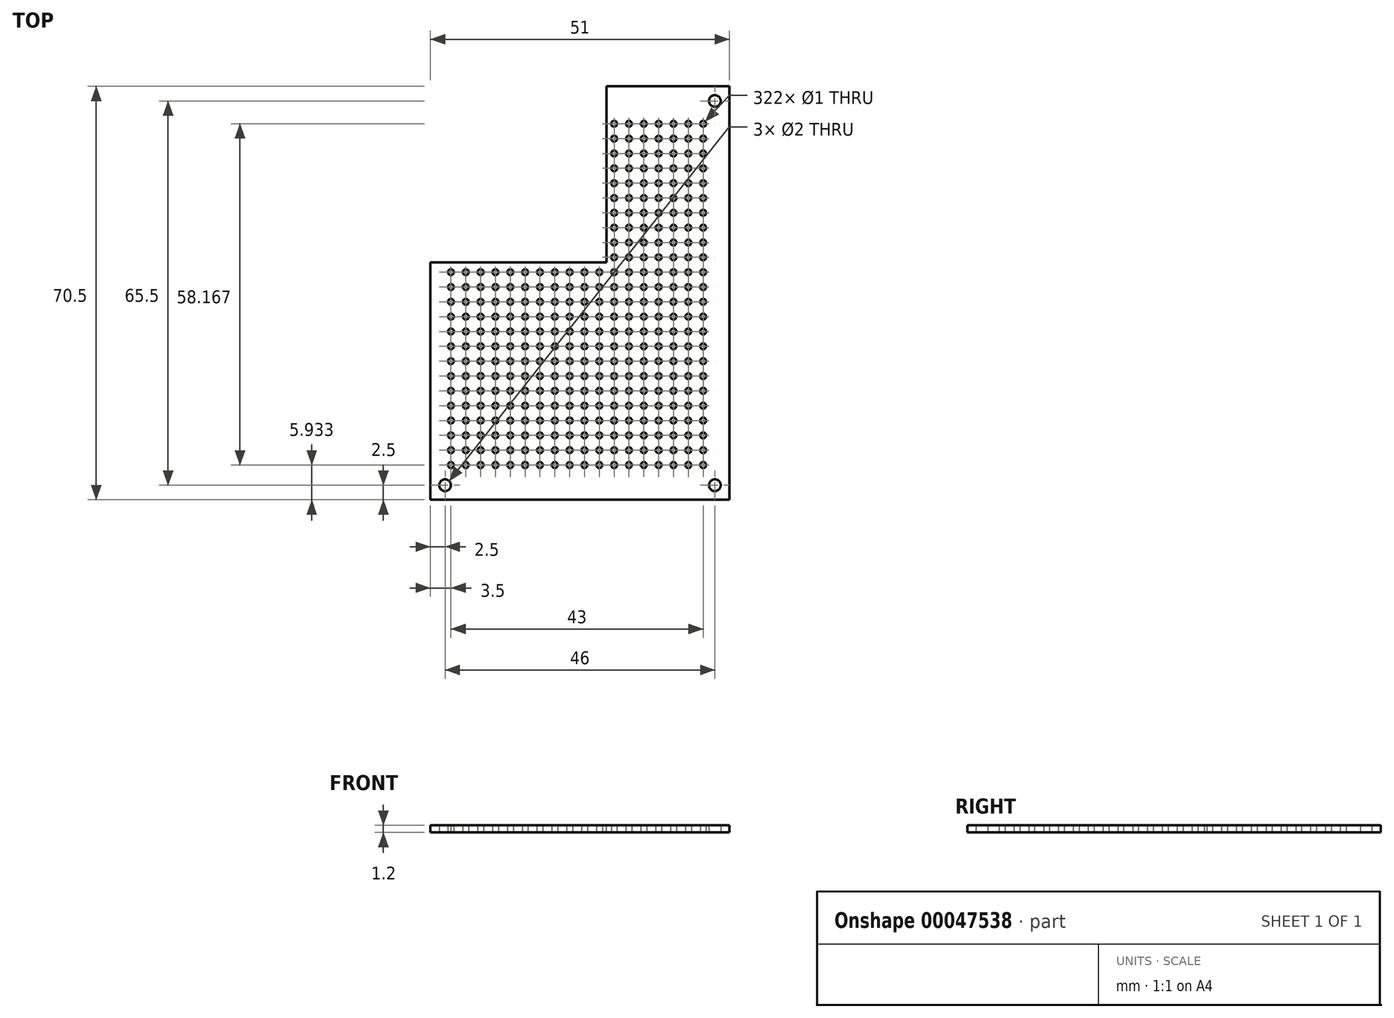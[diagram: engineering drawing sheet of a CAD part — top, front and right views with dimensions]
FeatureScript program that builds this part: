
annotation { "Feature Type Name" : "Feature", "Feature Type Description" : "" }
export const myFeature = defineFeature(function(context is Context, id is Id, definition is map)
    precondition{}
    {
        {
            var Q0;
            Q0=qCreatedBy(makeId("Top.planeOp"),FACE);
            var sketch = newSketch(context, id + "F0", { "sketchPlane" : qUnion([Q0])});
            skLineSegment(sketch, "E0.bottom", {"start": v(-25.5, 35.25) * mm, "end": v(25.5, 35.25) * mm});
            skLineSegment(sketch, "E0.top", {"start": v(-25.5, -35.25) * mm, "end": v(25.5, -35.25) * mm});
            skLineSegment(sketch, "E0.left", {"start": v(-25.5, 35.25) * mm, "end": v(-25.5, -35.25) * mm});
            skLineSegment(sketch, "E0.right", {"start": v(25.5, 35.25) * mm, "end": v(25.5, -35.25) * mm});
            skCircle(sketch, "E1", {"center": v(-23, 32.75) * mm, "radius": 1 * mm});
            skCircle(sketch, "E2", {"center": v(23, 32.75) * mm, "radius": 1 * mm});
            skCircle(sketch, "E3", {"center": v(23, -32.75) * mm, "radius": 1 * mm});
            skCircle(sketch, "E4", {"center": v(-23, -32.75) * mm, "radius": 1 * mm});
            skSolve(sketch);
        }
        {
            var Q0;
            Q0 = qSketchRegion(id + "F0", true);
            extrude(context, id + "F1", {"entities" : qUnion([Q0]), "depth" : 1.2 * mm});
        }
        {
            var Q0;
            Q0=qCreatedBy(makeId("Top.planeOp"),FACE);
            var sketch = newSketch(context, id + "F2", { "sketchPlane" : qUnion([Q0])});
            skCircle(sketch, "E5", {"center": v(-22, 28.85) * mm, "radius": 0.5 * mm});
            skCircle(sketch, "E6.1.0.0", {"center": v(-19.47, 28.85) * mm, "radius": 0.5 * mm});
            skCircle(sketch, "E6.2.0.0", {"center": v(-16.94, 28.85) * mm, "radius": 0.5 * mm});
            skCircle(sketch, "E6.3.0.0", {"center": v(-14.41, 28.85) * mm, "radius": 0.5 * mm});
            skCircle(sketch, "E6.4.0.0", {"center": v(-11.88, 28.85) * mm, "radius": 0.5 * mm});
            skCircle(sketch, "E6.5.0.0", {"center": v(-9.35, 28.85) * mm, "radius": 0.5 * mm});
            skCircle(sketch, "E6.6.0.0", {"center": v(-6.82, 28.85) * mm, "radius": 0.5 * mm});
            skCircle(sketch, "E6.7.0.0", {"center": v(-4.3, 28.85) * mm, "radius": 0.5 * mm});
            skCircle(sketch, "E6.8.0.0", {"center": v(-1.76, 28.85) * mm, "radius": 0.5 * mm});
            skCircle(sketch, "E6.9.0.0", {"center": v(0.76, 28.85) * mm, "radius": 0.5 * mm});
            skCircle(sketch, "E6.10.0.0", {"center": v(3.3, 28.85) * mm, "radius": 0.5 * mm});
            skCircle(sketch, "E6.11.0.0", {"center": v(5.82, 28.85) * mm, "radius": 0.5 * mm});
            skCircle(sketch, "E6.12.0.0", {"center": v(8.35, 28.85) * mm, "radius": 0.5 * mm});
            skCircle(sketch, "E6.13.0.0", {"center": v(10.88, 28.85) * mm, "radius": 0.5 * mm});
            skCircle(sketch, "E6.14.0.0", {"center": v(13.41, 28.85) * mm, "radius": 0.5 * mm});
            skCircle(sketch, "E6.15.0.0", {"center": v(15.94, 28.85) * mm, "radius": 0.5 * mm});
            skCircle(sketch, "E6.16.0.0", {"center": v(18.47, 28.85) * mm, "radius": 0.5 * mm});
            skCircle(sketch, "E6.17.0.0", {"center": v(21, 28.85) * mm, "radius": 0.5 * mm});
            skLineSegment(sketch, "E6.direction1", {"start": v(-22, 28.85) * mm, "end": v(-19.47, 28.85) * mm, "construction": true});
            skCircle(sketch, "E7.1.0.0", {"center": v(3.3, 26.32) * mm, "radius": 0.5 * mm});
            skCircle(sketch, "E7.1.0.1", {"center": v(5.82, 26.32) * mm, "radius": 0.5 * mm});
            skCircle(sketch, "E7.1.0.2", {"center": v(8.35, 26.32) * mm, "radius": 0.5 * mm});
            skCircle(sketch, "E7.1.0.3", {"center": v(18.47, 26.32) * mm, "radius": 0.5 * mm});
            skCircle(sketch, "E7.1.0.4", {"center": v(0.76, 26.32) * mm, "radius": 0.5 * mm});
            skCircle(sketch, "E7.1.0.5", {"center": v(10.88, 26.32) * mm, "radius": 0.5 * mm});
            skCircle(sketch, "E7.1.0.6", {"center": v(13.41, 26.32) * mm, "radius": 0.5 * mm});
            skCircle(sketch, "E7.1.0.7", {"center": v(15.94, 26.32) * mm, "radius": 0.5 * mm});
            skCircle(sketch, "E7.1.0.8", {"center": v(-16.94, 26.32) * mm, "radius": 0.5 * mm});
            skCircle(sketch, "E7.1.0.9", {"center": v(-14.41, 26.32) * mm, "radius": 0.5 * mm});
            skCircle(sketch, "E7.1.0.10", {"center": v(-11.88, 26.32) * mm, "radius": 0.5 * mm});
            skCircle(sketch, "E7.1.0.11", {"center": v(-9.35, 26.32) * mm, "radius": 0.5 * mm});
            skCircle(sketch, "E7.1.0.12", {"center": v(-6.82, 26.32) * mm, "radius": 0.5 * mm});
            skCircle(sketch, "E7.1.0.13", {"center": v(-4.3, 26.32) * mm, "radius": 0.5 * mm});
            skCircle(sketch, "E7.1.0.14", {"center": v(-1.76, 26.32) * mm, "radius": 0.5 * mm});
            skLineSegment(sketch, "E7.1.0.15", {"start": v(-22, 26.32) * mm, "end": v(-19.47, 26.32) * mm, "construction": true});
            skCircle(sketch, "E7.1.0.16", {"center": v(21, 26.32) * mm, "radius": 0.5 * mm});
            skCircle(sketch, "E7.1.0.17", {"center": v(-22, 26.32) * mm, "radius": 0.5 * mm});
            skCircle(sketch, "E7.1.0.18", {"center": v(-19.47, 26.32) * mm, "radius": 0.5 * mm});
            skCircle(sketch, "E7.2.0.0", {"center": v(3.3, 23.8) * mm, "radius": 0.5 * mm});
            skCircle(sketch, "E7.2.0.1", {"center": v(5.82, 23.8) * mm, "radius": 0.5 * mm});
            skCircle(sketch, "E7.2.0.2", {"center": v(8.35, 23.8) * mm, "radius": 0.5 * mm});
            skCircle(sketch, "E7.2.0.3", {"center": v(18.47, 23.8) * mm, "radius": 0.5 * mm});
            skCircle(sketch, "E7.2.0.4", {"center": v(0.76, 23.8) * mm, "radius": 0.5 * mm});
            skCircle(sketch, "E7.2.0.5", {"center": v(10.88, 23.8) * mm, "radius": 0.5 * mm});
            skCircle(sketch, "E7.2.0.6", {"center": v(13.41, 23.8) * mm, "radius": 0.5 * mm});
            skCircle(sketch, "E7.2.0.7", {"center": v(15.94, 23.8) * mm, "radius": 0.5 * mm});
            skCircle(sketch, "E7.2.0.8", {"center": v(-16.94, 23.8) * mm, "radius": 0.5 * mm});
            skCircle(sketch, "E7.2.0.9", {"center": v(-14.41, 23.8) * mm, "radius": 0.5 * mm});
            skCircle(sketch, "E7.2.0.10", {"center": v(-11.88, 23.8) * mm, "radius": 0.5 * mm});
            skCircle(sketch, "E7.2.0.11", {"center": v(-9.35, 23.8) * mm, "radius": 0.5 * mm});
            skCircle(sketch, "E7.2.0.12", {"center": v(-6.82, 23.8) * mm, "radius": 0.5 * mm});
            skCircle(sketch, "E7.2.0.13", {"center": v(-4.3, 23.8) * mm, "radius": 0.5 * mm});
            skCircle(sketch, "E7.2.0.14", {"center": v(-1.76, 23.8) * mm, "radius": 0.5 * mm});
            skLineSegment(sketch, "E7.2.0.15", {"start": v(-22, 23.8) * mm, "end": v(-19.47, 23.8) * mm, "construction": true});
            skCircle(sketch, "E7.2.0.16", {"center": v(21, 23.8) * mm, "radius": 0.5 * mm});
            skCircle(sketch, "E7.2.0.17", {"center": v(-22, 23.8) * mm, "radius": 0.5 * mm});
            skCircle(sketch, "E7.2.0.18", {"center": v(-19.47, 23.8) * mm, "radius": 0.5 * mm});
            skCircle(sketch, "E7.3.0.0", {"center": v(3.3, 21.26) * mm, "radius": 0.5 * mm});
            skCircle(sketch, "E7.3.0.1", {"center": v(5.82, 21.26) * mm, "radius": 0.5 * mm});
            skCircle(sketch, "E7.3.0.2", {"center": v(8.35, 21.26) * mm, "radius": 0.5 * mm});
            skCircle(sketch, "E7.3.0.3", {"center": v(18.47, 21.26) * mm, "radius": 0.5 * mm});
            skCircle(sketch, "E7.3.0.4", {"center": v(0.76, 21.26) * mm, "radius": 0.5 * mm});
            skCircle(sketch, "E7.3.0.5", {"center": v(10.88, 21.26) * mm, "radius": 0.5 * mm});
            skCircle(sketch, "E7.3.0.6", {"center": v(13.41, 21.26) * mm, "radius": 0.5 * mm});
            skCircle(sketch, "E7.3.0.7", {"center": v(15.94, 21.26) * mm, "radius": 0.5 * mm});
            skCircle(sketch, "E7.3.0.8", {"center": v(-16.94, 21.26) * mm, "radius": 0.5 * mm});
            skCircle(sketch, "E7.3.0.9", {"center": v(-14.41, 21.26) * mm, "radius": 0.5 * mm});
            skCircle(sketch, "E7.3.0.10", {"center": v(-11.88, 21.26) * mm, "radius": 0.5 * mm});
            skCircle(sketch, "E7.3.0.11", {"center": v(-9.35, 21.26) * mm, "radius": 0.5 * mm});
            skCircle(sketch, "E7.3.0.12", {"center": v(-6.82, 21.26) * mm, "radius": 0.5 * mm});
            skCircle(sketch, "E7.3.0.13", {"center": v(-4.3, 21.26) * mm, "radius": 0.5 * mm});
            skCircle(sketch, "E7.3.0.14", {"center": v(-1.76, 21.26) * mm, "radius": 0.5 * mm});
            skLineSegment(sketch, "E7.3.0.15", {"start": v(-22, 21.26) * mm, "end": v(-19.47, 21.26) * mm, "construction": true});
            skCircle(sketch, "E7.3.0.16", {"center": v(21, 21.26) * mm, "radius": 0.5 * mm});
            skCircle(sketch, "E7.3.0.17", {"center": v(-22, 21.26) * mm, "radius": 0.5 * mm});
            skCircle(sketch, "E7.3.0.18", {"center": v(-19.47, 21.26) * mm, "radius": 0.5 * mm});
            skCircle(sketch, "E7.4.0.0", {"center": v(3.3, 18.73) * mm, "radius": 0.5 * mm});
            skCircle(sketch, "E7.4.0.1", {"center": v(5.82, 18.73) * mm, "radius": 0.5 * mm});
            skCircle(sketch, "E7.4.0.2", {"center": v(8.35, 18.73) * mm, "radius": 0.5 * mm});
            skCircle(sketch, "E7.4.0.3", {"center": v(18.47, 18.73) * mm, "radius": 0.5 * mm});
            skCircle(sketch, "E7.4.0.4", {"center": v(0.76, 18.73) * mm, "radius": 0.5 * mm});
            skCircle(sketch, "E7.4.0.5", {"center": v(10.88, 18.73) * mm, "radius": 0.5 * mm});
            skCircle(sketch, "E7.4.0.6", {"center": v(13.41, 18.73) * mm, "radius": 0.5 * mm});
            skCircle(sketch, "E7.4.0.7", {"center": v(15.94, 18.73) * mm, "radius": 0.5 * mm});
            skCircle(sketch, "E7.4.0.8", {"center": v(-16.94, 18.73) * mm, "radius": 0.5 * mm});
            skCircle(sketch, "E7.4.0.9", {"center": v(-14.41, 18.73) * mm, "radius": 0.5 * mm});
            skCircle(sketch, "E7.4.0.10", {"center": v(-11.88, 18.73) * mm, "radius": 0.5 * mm});
            skCircle(sketch, "E7.4.0.11", {"center": v(-9.35, 18.73) * mm, "radius": 0.5 * mm});
            skCircle(sketch, "E7.4.0.12", {"center": v(-6.82, 18.73) * mm, "radius": 0.5 * mm});
            skCircle(sketch, "E7.4.0.13", {"center": v(-4.3, 18.73) * mm, "radius": 0.5 * mm});
            skCircle(sketch, "E7.4.0.14", {"center": v(-1.76, 18.73) * mm, "radius": 0.5 * mm});
            skLineSegment(sketch, "E7.4.0.15", {"start": v(-22, 18.73) * mm, "end": v(-19.47, 18.73) * mm, "construction": true});
            skCircle(sketch, "E7.4.0.16", {"center": v(21, 18.73) * mm, "radius": 0.5 * mm});
            skCircle(sketch, "E7.4.0.17", {"center": v(-22, 18.73) * mm, "radius": 0.5 * mm});
            skCircle(sketch, "E7.4.0.18", {"center": v(-19.47, 18.73) * mm, "radius": 0.5 * mm});
            skCircle(sketch, "E7.5.0.0", {"center": v(3.3, 16.2) * mm, "radius": 0.5 * mm});
            skCircle(sketch, "E7.5.0.1", {"center": v(5.82, 16.2) * mm, "radius": 0.5 * mm});
            skCircle(sketch, "E7.5.0.2", {"center": v(8.35, 16.2) * mm, "radius": 0.5 * mm});
            skCircle(sketch, "E7.5.0.3", {"center": v(18.47, 16.2) * mm, "radius": 0.5 * mm});
            skCircle(sketch, "E7.5.0.4", {"center": v(0.76, 16.2) * mm, "radius": 0.5 * mm});
            skCircle(sketch, "E7.5.0.5", {"center": v(10.88, 16.2) * mm, "radius": 0.5 * mm});
            skCircle(sketch, "E7.5.0.6", {"center": v(13.41, 16.2) * mm, "radius": 0.5 * mm});
            skCircle(sketch, "E7.5.0.7", {"center": v(15.94, 16.2) * mm, "radius": 0.5 * mm});
            skCircle(sketch, "E7.5.0.8", {"center": v(-16.94, 16.2) * mm, "radius": 0.5 * mm});
            skCircle(sketch, "E7.5.0.9", {"center": v(-14.41, 16.2) * mm, "radius": 0.5 * mm});
            skCircle(sketch, "E7.5.0.10", {"center": v(-11.88, 16.2) * mm, "radius": 0.5 * mm});
            skCircle(sketch, "E7.5.0.11", {"center": v(-9.35, 16.2) * mm, "radius": 0.5 * mm});
            skCircle(sketch, "E7.5.0.12", {"center": v(-6.82, 16.2) * mm, "radius": 0.5 * mm});
            skCircle(sketch, "E7.5.0.13", {"center": v(-4.3, 16.2) * mm, "radius": 0.5 * mm});
            skCircle(sketch, "E7.5.0.14", {"center": v(-1.76, 16.2) * mm, "radius": 0.5 * mm});
            skLineSegment(sketch, "E7.5.0.15", {"start": v(-22, 16.2) * mm, "end": v(-19.47, 16.2) * mm, "construction": true});
            skCircle(sketch, "E7.5.0.16", {"center": v(21, 16.2) * mm, "radius": 0.5 * mm});
            skCircle(sketch, "E7.5.0.17", {"center": v(-22, 16.2) * mm, "radius": 0.5 * mm});
            skCircle(sketch, "E7.5.0.18", {"center": v(-19.47, 16.2) * mm, "radius": 0.5 * mm});
            skCircle(sketch, "E7.6.0.0", {"center": v(3.3, 13.68) * mm, "radius": 0.5 * mm});
            skCircle(sketch, "E7.6.0.1", {"center": v(5.82, 13.68) * mm, "radius": 0.5 * mm});
            skCircle(sketch, "E7.6.0.2", {"center": v(8.35, 13.68) * mm, "radius": 0.5 * mm});
            skCircle(sketch, "E7.6.0.3", {"center": v(18.47, 13.68) * mm, "radius": 0.5 * mm});
            skCircle(sketch, "E7.6.0.4", {"center": v(0.76, 13.68) * mm, "radius": 0.5 * mm});
            skCircle(sketch, "E7.6.0.5", {"center": v(10.88, 13.68) * mm, "radius": 0.5 * mm});
            skCircle(sketch, "E7.6.0.6", {"center": v(13.41, 13.68) * mm, "radius": 0.5 * mm});
            skCircle(sketch, "E7.6.0.7", {"center": v(15.94, 13.68) * mm, "radius": 0.5 * mm});
            skCircle(sketch, "E7.6.0.8", {"center": v(-16.94, 13.68) * mm, "radius": 0.5 * mm});
            skCircle(sketch, "E7.6.0.9", {"center": v(-14.41, 13.68) * mm, "radius": 0.5 * mm});
            skCircle(sketch, "E7.6.0.10", {"center": v(-11.88, 13.68) * mm, "radius": 0.5 * mm});
            skCircle(sketch, "E7.6.0.11", {"center": v(-9.35, 13.68) * mm, "radius": 0.5 * mm});
            skCircle(sketch, "E7.6.0.12", {"center": v(-6.82, 13.68) * mm, "radius": 0.5 * mm});
            skCircle(sketch, "E7.6.0.13", {"center": v(-4.3, 13.68) * mm, "radius": 0.5 * mm});
            skCircle(sketch, "E7.6.0.14", {"center": v(-1.76, 13.68) * mm, "radius": 0.5 * mm});
            skLineSegment(sketch, "E7.6.0.15", {"start": v(-22, 13.68) * mm, "end": v(-19.47, 13.68) * mm, "construction": true});
            skCircle(sketch, "E7.6.0.16", {"center": v(21, 13.68) * mm, "radius": 0.5 * mm});
            skCircle(sketch, "E7.6.0.17", {"center": v(-22, 13.68) * mm, "radius": 0.5 * mm});
            skCircle(sketch, "E7.6.0.18", {"center": v(-19.47, 13.68) * mm, "radius": 0.5 * mm});
            skCircle(sketch, "E7.7.0.0", {"center": v(3.3, 11.15) * mm, "radius": 0.5 * mm});
            skCircle(sketch, "E7.7.0.1", {"center": v(5.82, 11.15) * mm, "radius": 0.5 * mm});
            skCircle(sketch, "E7.7.0.2", {"center": v(8.35, 11.15) * mm, "radius": 0.5 * mm});
            skCircle(sketch, "E7.7.0.3", {"center": v(18.47, 11.15) * mm, "radius": 0.5 * mm});
            skCircle(sketch, "E7.7.0.4", {"center": v(0.76, 11.15) * mm, "radius": 0.5 * mm});
            skCircle(sketch, "E7.7.0.5", {"center": v(10.88, 11.15) * mm, "radius": 0.5 * mm});
            skCircle(sketch, "E7.7.0.6", {"center": v(13.41, 11.15) * mm, "radius": 0.5 * mm});
            skCircle(sketch, "E7.7.0.7", {"center": v(15.94, 11.15) * mm, "radius": 0.5 * mm});
            skCircle(sketch, "E7.7.0.8", {"center": v(-16.94, 11.15) * mm, "radius": 0.5 * mm});
            skCircle(sketch, "E7.7.0.9", {"center": v(-14.41, 11.15) * mm, "radius": 0.5 * mm});
            skCircle(sketch, "E7.7.0.10", {"center": v(-11.88, 11.15) * mm, "radius": 0.5 * mm});
            skCircle(sketch, "E7.7.0.11", {"center": v(-9.35, 11.15) * mm, "radius": 0.5 * mm});
            skCircle(sketch, "E7.7.0.12", {"center": v(-6.82, 11.15) * mm, "radius": 0.5 * mm});
            skCircle(sketch, "E7.7.0.13", {"center": v(-4.3, 11.15) * mm, "radius": 0.5 * mm});
            skCircle(sketch, "E7.7.0.14", {"center": v(-1.76, 11.15) * mm, "radius": 0.5 * mm});
            skLineSegment(sketch, "E7.7.0.15", {"start": v(-22, 11.15) * mm, "end": v(-19.47, 11.15) * mm, "construction": true});
            skCircle(sketch, "E7.7.0.16", {"center": v(21, 11.15) * mm, "radius": 0.5 * mm});
            skCircle(sketch, "E7.7.0.17", {"center": v(-22, 11.15) * mm, "radius": 0.5 * mm});
            skCircle(sketch, "E7.7.0.18", {"center": v(-19.47, 11.15) * mm, "radius": 0.5 * mm});
            skCircle(sketch, "E7.8.0.0", {"center": v(3.3, 8.62) * mm, "radius": 0.5 * mm});
            skCircle(sketch, "E7.8.0.1", {"center": v(5.82, 8.62) * mm, "radius": 0.5 * mm});
            skCircle(sketch, "E7.8.0.2", {"center": v(8.35, 8.62) * mm, "radius": 0.5 * mm});
            skCircle(sketch, "E7.8.0.3", {"center": v(18.47, 8.62) * mm, "radius": 0.5 * mm});
            skCircle(sketch, "E7.8.0.4", {"center": v(0.76, 8.62) * mm, "radius": 0.5 * mm});
            skCircle(sketch, "E7.8.0.5", {"center": v(10.88, 8.62) * mm, "radius": 0.5 * mm});
            skCircle(sketch, "E7.8.0.6", {"center": v(13.41, 8.62) * mm, "radius": 0.5 * mm});
            skCircle(sketch, "E7.8.0.7", {"center": v(15.94, 8.62) * mm, "radius": 0.5 * mm});
            skCircle(sketch, "E7.8.0.8", {"center": v(-16.94, 8.62) * mm, "radius": 0.5 * mm});
            skCircle(sketch, "E7.8.0.9", {"center": v(-14.41, 8.62) * mm, "radius": 0.5 * mm});
            skCircle(sketch, "E7.8.0.10", {"center": v(-11.88, 8.62) * mm, "radius": 0.5 * mm});
            skCircle(sketch, "E7.8.0.11", {"center": v(-9.35, 8.62) * mm, "radius": 0.5 * mm});
            skCircle(sketch, "E7.8.0.12", {"center": v(-6.82, 8.62) * mm, "radius": 0.5 * mm});
            skCircle(sketch, "E7.8.0.13", {"center": v(-4.3, 8.62) * mm, "radius": 0.5 * mm});
            skCircle(sketch, "E7.8.0.14", {"center": v(-1.76, 8.62) * mm, "radius": 0.5 * mm});
            skLineSegment(sketch, "E7.8.0.15", {"start": v(-22, 8.62) * mm, "end": v(-19.47, 8.62) * mm, "construction": true});
            skCircle(sketch, "E7.8.0.16", {"center": v(21, 8.62) * mm, "radius": 0.5 * mm});
            skCircle(sketch, "E7.8.0.17", {"center": v(-22, 8.62) * mm, "radius": 0.5 * mm});
            skCircle(sketch, "E7.8.0.18", {"center": v(-19.47, 8.62) * mm, "radius": 0.5 * mm});
            skCircle(sketch, "E7.9.0.0", {"center": v(3.3, 6.09) * mm, "radius": 0.5 * mm});
            skCircle(sketch, "E7.9.0.1", {"center": v(5.82, 6.09) * mm, "radius": 0.5 * mm});
            skCircle(sketch, "E7.9.0.2", {"center": v(8.35, 6.09) * mm, "radius": 0.5 * mm});
            skCircle(sketch, "E7.9.0.3", {"center": v(18.47, 6.09) * mm, "radius": 0.5 * mm});
            skCircle(sketch, "E7.9.0.4", {"center": v(0.76, 6.09) * mm, "radius": 0.5 * mm});
            skCircle(sketch, "E7.9.0.5", {"center": v(10.88, 6.09) * mm, "radius": 0.5 * mm});
            skCircle(sketch, "E7.9.0.6", {"center": v(13.41, 6.09) * mm, "radius": 0.5 * mm});
            skCircle(sketch, "E7.9.0.7", {"center": v(15.94, 6.09) * mm, "radius": 0.5 * mm});
            skCircle(sketch, "E7.9.0.8", {"center": v(-16.94, 6.09) * mm, "radius": 0.5 * mm});
            skCircle(sketch, "E7.9.0.9", {"center": v(-14.41, 6.09) * mm, "radius": 0.5 * mm});
            skCircle(sketch, "E7.9.0.10", {"center": v(-11.88, 6.09) * mm, "radius": 0.5 * mm});
            skCircle(sketch, "E7.9.0.11", {"center": v(-9.35, 6.09) * mm, "radius": 0.5 * mm});
            skCircle(sketch, "E7.9.0.12", {"center": v(-6.82, 6.09) * mm, "radius": 0.5 * mm});
            skCircle(sketch, "E7.9.0.13", {"center": v(-4.3, 6.09) * mm, "radius": 0.5 * mm});
            skCircle(sketch, "E7.9.0.14", {"center": v(-1.76, 6.09) * mm, "radius": 0.5 * mm});
            skLineSegment(sketch, "E7.9.0.15", {"start": v(-22, 6.09) * mm, "end": v(-19.47, 6.09) * mm, "construction": true});
            skCircle(sketch, "E7.9.0.16", {"center": v(21, 6.09) * mm, "radius": 0.5 * mm});
            skCircle(sketch, "E7.9.0.17", {"center": v(-22, 6.09) * mm, "radius": 0.5 * mm});
            skCircle(sketch, "E7.9.0.18", {"center": v(-19.47, 6.09) * mm, "radius": 0.5 * mm});
            skCircle(sketch, "E7.10.0.0", {"center": v(3.3, 3.56) * mm, "radius": 0.5 * mm});
            skCircle(sketch, "E7.10.0.1", {"center": v(5.82, 3.56) * mm, "radius": 0.5 * mm});
            skCircle(sketch, "E7.10.0.2", {"center": v(8.35, 3.56) * mm, "radius": 0.5 * mm});
            skCircle(sketch, "E7.10.0.3", {"center": v(18.47, 3.56) * mm, "radius": 0.5 * mm});
            skCircle(sketch, "E7.10.0.4", {"center": v(0.76, 3.56) * mm, "radius": 0.5 * mm});
            skCircle(sketch, "E7.10.0.5", {"center": v(10.88, 3.56) * mm, "radius": 0.5 * mm});
            skCircle(sketch, "E7.10.0.6", {"center": v(13.41, 3.56) * mm, "radius": 0.5 * mm});
            skCircle(sketch, "E7.10.0.7", {"center": v(15.94, 3.56) * mm, "radius": 0.5 * mm});
            skCircle(sketch, "E7.10.0.8", {"center": v(-16.94, 3.56) * mm, "radius": 0.5 * mm});
            skCircle(sketch, "E7.10.0.9", {"center": v(-14.41, 3.56) * mm, "radius": 0.5 * mm});
            skCircle(sketch, "E7.10.0.10", {"center": v(-11.88, 3.56) * mm, "radius": 0.5 * mm});
            skCircle(sketch, "E7.10.0.11", {"center": v(-9.35, 3.56) * mm, "radius": 0.5 * mm});
            skCircle(sketch, "E7.10.0.12", {"center": v(-6.82, 3.56) * mm, "radius": 0.5 * mm});
            skCircle(sketch, "E7.10.0.13", {"center": v(-4.3, 3.56) * mm, "radius": 0.5 * mm});
            skCircle(sketch, "E7.10.0.14", {"center": v(-1.76, 3.56) * mm, "radius": 0.5 * mm});
            skLineSegment(sketch, "E7.10.0.15", {"start": v(-22, 3.56) * mm, "end": v(-19.47, 3.56) * mm, "construction": true});
            skCircle(sketch, "E7.10.0.16", {"center": v(21, 3.56) * mm, "radius": 0.5 * mm});
            skCircle(sketch, "E7.10.0.17", {"center": v(-22, 3.56) * mm, "radius": 0.5 * mm});
            skCircle(sketch, "E7.10.0.18", {"center": v(-19.47, 3.56) * mm, "radius": 0.5 * mm});
            skCircle(sketch, "E7.11.0.0", {"center": v(3.3, 1.03) * mm, "radius": 0.5 * mm});
            skCircle(sketch, "E7.11.0.1", {"center": v(5.82, 1.03) * mm, "radius": 0.5 * mm});
            skCircle(sketch, "E7.11.0.2", {"center": v(8.35, 1.03) * mm, "radius": 0.5 * mm});
            skCircle(sketch, "E7.11.0.3", {"center": v(18.47, 1.03) * mm, "radius": 0.5 * mm});
            skCircle(sketch, "E7.11.0.4", {"center": v(0.76, 1.03) * mm, "radius": 0.5 * mm});
            skCircle(sketch, "E7.11.0.5", {"center": v(10.88, 1.03) * mm, "radius": 0.5 * mm});
            skCircle(sketch, "E7.11.0.6", {"center": v(13.41, 1.03) * mm, "radius": 0.5 * mm});
            skCircle(sketch, "E7.11.0.7", {"center": v(15.94, 1.03) * mm, "radius": 0.5 * mm});
            skCircle(sketch, "E7.11.0.8", {"center": v(-16.94, 1.03) * mm, "radius": 0.5 * mm});
            skCircle(sketch, "E7.11.0.9", {"center": v(-14.41, 1.03) * mm, "radius": 0.5 * mm});
            skCircle(sketch, "E7.11.0.10", {"center": v(-11.88, 1.03) * mm, "radius": 0.5 * mm});
            skCircle(sketch, "E7.11.0.11", {"center": v(-9.35, 1.03) * mm, "radius": 0.5 * mm});
            skCircle(sketch, "E7.11.0.12", {"center": v(-6.82, 1.03) * mm, "radius": 0.5 * mm});
            skCircle(sketch, "E7.11.0.13", {"center": v(-4.3, 1.03) * mm, "radius": 0.5 * mm});
            skCircle(sketch, "E7.11.0.14", {"center": v(-1.76, 1.03) * mm, "radius": 0.5 * mm});
            skLineSegment(sketch, "E7.11.0.15", {"start": v(-22, 1.03) * mm, "end": v(-19.47, 1.03) * mm, "construction": true});
            skCircle(sketch, "E7.11.0.16", {"center": v(21, 1.03) * mm, "radius": 0.5 * mm});
            skCircle(sketch, "E7.11.0.17", {"center": v(-22, 1.03) * mm, "radius": 0.5 * mm});
            skCircle(sketch, "E7.11.0.18", {"center": v(-19.47, 1.03) * mm, "radius": 0.5 * mm});
            skCircle(sketch, "E7.12.0.0", {"center": v(3.3, -1.5) * mm, "radius": 0.5 * mm});
            skCircle(sketch, "E7.12.0.1", {"center": v(5.82, -1.5) * mm, "radius": 0.5 * mm});
            skCircle(sketch, "E7.12.0.2", {"center": v(8.35, -1.5) * mm, "radius": 0.5 * mm});
            skCircle(sketch, "E7.12.0.3", {"center": v(18.47, -1.5) * mm, "radius": 0.5 * mm});
            skCircle(sketch, "E7.12.0.4", {"center": v(0.76, -1.5) * mm, "radius": 0.5 * mm});
            skCircle(sketch, "E7.12.0.5", {"center": v(10.88, -1.5) * mm, "radius": 0.5 * mm});
            skCircle(sketch, "E7.12.0.6", {"center": v(13.41, -1.5) * mm, "radius": 0.5 * mm});
            skCircle(sketch, "E7.12.0.7", {"center": v(15.94, -1.5) * mm, "radius": 0.5 * mm});
            skCircle(sketch, "E7.12.0.8", {"center": v(-16.94, -1.5) * mm, "radius": 0.5 * mm});
            skCircle(sketch, "E7.12.0.9", {"center": v(-14.41, -1.5) * mm, "radius": 0.5 * mm});
            skCircle(sketch, "E7.12.0.10", {"center": v(-11.88, -1.5) * mm, "radius": 0.5 * mm});
            skCircle(sketch, "E7.12.0.11", {"center": v(-9.35, -1.5) * mm, "radius": 0.5 * mm});
            skCircle(sketch, "E7.12.0.12", {"center": v(-6.82, -1.5) * mm, "radius": 0.5 * mm});
            skCircle(sketch, "E7.12.0.13", {"center": v(-4.3, -1.5) * mm, "radius": 0.5 * mm});
            skCircle(sketch, "E7.12.0.14", {"center": v(-1.76, -1.5) * mm, "radius": 0.5 * mm});
            skLineSegment(sketch, "E7.12.0.15", {"start": v(-22, -1.5) * mm, "end": v(-19.47, -1.5) * mm, "construction": true});
            skCircle(sketch, "E7.12.0.16", {"center": v(21, -1.5) * mm, "radius": 0.5 * mm});
            skCircle(sketch, "E7.12.0.17", {"center": v(-22, -1.5) * mm, "radius": 0.5 * mm});
            skCircle(sketch, "E7.12.0.18", {"center": v(-19.47, -1.5) * mm, "radius": 0.5 * mm});
            skCircle(sketch, "E7.13.0.0", {"center": v(3.3, -4.03) * mm, "radius": 0.5 * mm});
            skCircle(sketch, "E7.13.0.1", {"center": v(5.82, -4.03) * mm, "radius": 0.5 * mm});
            skCircle(sketch, "E7.13.0.2", {"center": v(8.35, -4.03) * mm, "radius": 0.5 * mm});
            skCircle(sketch, "E7.13.0.3", {"center": v(18.47, -4.03) * mm, "radius": 0.5 * mm});
            skCircle(sketch, "E7.13.0.4", {"center": v(0.76, -4.03) * mm, "radius": 0.5 * mm});
            skCircle(sketch, "E7.13.0.5", {"center": v(10.88, -4.03) * mm, "radius": 0.5 * mm});
            skCircle(sketch, "E7.13.0.6", {"center": v(13.41, -4.03) * mm, "radius": 0.5 * mm});
            skCircle(sketch, "E7.13.0.7", {"center": v(15.94, -4.03) * mm, "radius": 0.5 * mm});
            skCircle(sketch, "E7.13.0.8", {"center": v(-16.94, -4.03) * mm, "radius": 0.5 * mm});
            skCircle(sketch, "E7.13.0.9", {"center": v(-14.41, -4.03) * mm, "radius": 0.5 * mm});
            skCircle(sketch, "E7.13.0.10", {"center": v(-11.88, -4.03) * mm, "radius": 0.5 * mm});
            skCircle(sketch, "E7.13.0.11", {"center": v(-9.35, -4.03) * mm, "radius": 0.5 * mm});
            skCircle(sketch, "E7.13.0.12", {"center": v(-6.82, -4.03) * mm, "radius": 0.5 * mm});
            skCircle(sketch, "E7.13.0.13", {"center": v(-4.3, -4.03) * mm, "radius": 0.5 * mm});
            skCircle(sketch, "E7.13.0.14", {"center": v(-1.76, -4.03) * mm, "radius": 0.5 * mm});
            skLineSegment(sketch, "E7.13.0.15", {"start": v(-22, -4.03) * mm, "end": v(-19.47, -4.03) * mm, "construction": true});
            skCircle(sketch, "E7.13.0.16", {"center": v(21, -4.03) * mm, "radius": 0.5 * mm});
            skCircle(sketch, "E7.13.0.17", {"center": v(-22, -4.03) * mm, "radius": 0.5 * mm});
            skCircle(sketch, "E7.13.0.18", {"center": v(-19.47, -4.03) * mm, "radius": 0.5 * mm});
            skCircle(sketch, "E7.14.0.0", {"center": v(3.3, -6.56) * mm, "radius": 0.5 * mm});
            skCircle(sketch, "E7.14.0.1", {"center": v(5.82, -6.56) * mm, "radius": 0.5 * mm});
            skCircle(sketch, "E7.14.0.2", {"center": v(8.35, -6.56) * mm, "radius": 0.5 * mm});
            skCircle(sketch, "E7.14.0.3", {"center": v(18.47, -6.56) * mm, "radius": 0.5 * mm});
            skCircle(sketch, "E7.14.0.4", {"center": v(0.76, -6.56) * mm, "radius": 0.5 * mm});
            skCircle(sketch, "E7.14.0.5", {"center": v(10.88, -6.56) * mm, "radius": 0.5 * mm});
            skCircle(sketch, "E7.14.0.6", {"center": v(13.41, -6.56) * mm, "radius": 0.5 * mm});
            skCircle(sketch, "E7.14.0.7", {"center": v(15.94, -6.56) * mm, "radius": 0.5 * mm});
            skCircle(sketch, "E7.14.0.8", {"center": v(-16.94, -6.56) * mm, "radius": 0.5 * mm});
            skCircle(sketch, "E7.14.0.9", {"center": v(-14.41, -6.56) * mm, "radius": 0.5 * mm});
            skCircle(sketch, "E7.14.0.10", {"center": v(-11.88, -6.56) * mm, "radius": 0.5 * mm});
            skCircle(sketch, "E7.14.0.11", {"center": v(-9.35, -6.56) * mm, "radius": 0.5 * mm});
            skCircle(sketch, "E7.14.0.12", {"center": v(-6.82, -6.56) * mm, "radius": 0.5 * mm});
            skCircle(sketch, "E7.14.0.13", {"center": v(-4.3, -6.56) * mm, "radius": 0.5 * mm});
            skCircle(sketch, "E7.14.0.14", {"center": v(-1.76, -6.56) * mm, "radius": 0.5 * mm});
            skLineSegment(sketch, "E7.14.0.15", {"start": v(-22, -6.56) * mm, "end": v(-19.47, -6.56) * mm, "construction": true});
            skCircle(sketch, "E7.14.0.16", {"center": v(21, -6.56) * mm, "radius": 0.5 * mm});
            skCircle(sketch, "E7.14.0.17", {"center": v(-22, -6.56) * mm, "radius": 0.5 * mm});
            skCircle(sketch, "E7.14.0.18", {"center": v(-19.47, -6.56) * mm, "radius": 0.5 * mm});
            skCircle(sketch, "E7.15.0.0", {"center": v(3.3, -9.08) * mm, "radius": 0.5 * mm});
            skCircle(sketch, "E7.15.0.1", {"center": v(5.82, -9.08) * mm, "radius": 0.5 * mm});
            skCircle(sketch, "E7.15.0.2", {"center": v(8.35, -9.08) * mm, "radius": 0.5 * mm});
            skCircle(sketch, "E7.15.0.3", {"center": v(18.47, -9.08) * mm, "radius": 0.5 * mm});
            skCircle(sketch, "E7.15.0.4", {"center": v(0.76, -9.08) * mm, "radius": 0.5 * mm});
            skCircle(sketch, "E7.15.0.5", {"center": v(10.88, -9.08) * mm, "radius": 0.5 * mm});
            skCircle(sketch, "E7.15.0.6", {"center": v(13.41, -9.08) * mm, "radius": 0.5 * mm});
            skCircle(sketch, "E7.15.0.7", {"center": v(15.94, -9.08) * mm, "radius": 0.5 * mm});
            skCircle(sketch, "E7.15.0.8", {"center": v(-16.94, -9.08) * mm, "radius": 0.5 * mm});
            skCircle(sketch, "E7.15.0.9", {"center": v(-14.41, -9.08) * mm, "radius": 0.5 * mm});
            skCircle(sketch, "E7.15.0.10", {"center": v(-11.88, -9.08) * mm, "radius": 0.5 * mm});
            skCircle(sketch, "E7.15.0.11", {"center": v(-9.35, -9.08) * mm, "radius": 0.5 * mm});
            skCircle(sketch, "E7.15.0.12", {"center": v(-6.82, -9.08) * mm, "radius": 0.5 * mm});
            skCircle(sketch, "E7.15.0.13", {"center": v(-4.3, -9.08) * mm, "radius": 0.5 * mm});
            skCircle(sketch, "E7.15.0.14", {"center": v(-1.76, -9.08) * mm, "radius": 0.5 * mm});
            skLineSegment(sketch, "E7.15.0.15", {"start": v(-22, -9.08) * mm, "end": v(-19.47, -9.08) * mm, "construction": true});
            skCircle(sketch, "E7.15.0.16", {"center": v(21, -9.08) * mm, "radius": 0.5 * mm});
            skCircle(sketch, "E7.15.0.17", {"center": v(-22, -9.08) * mm, "radius": 0.5 * mm});
            skCircle(sketch, "E7.15.0.18", {"center": v(-19.47, -9.08) * mm, "radius": 0.5 * mm});
            skCircle(sketch, "E7.16.0.0", {"center": v(3.3, -11.61) * mm, "radius": 0.5 * mm});
            skCircle(sketch, "E7.16.0.1", {"center": v(5.82, -11.61) * mm, "radius": 0.5 * mm});
            skCircle(sketch, "E7.16.0.2", {"center": v(8.35, -11.61) * mm, "radius": 0.5 * mm});
            skCircle(sketch, "E7.16.0.3", {"center": v(18.47, -11.61) * mm, "radius": 0.5 * mm});
            skCircle(sketch, "E7.16.0.4", {"center": v(0.76, -11.61) * mm, "radius": 0.5 * mm});
            skCircle(sketch, "E7.16.0.5", {"center": v(10.88, -11.61) * mm, "radius": 0.5 * mm});
            skCircle(sketch, "E7.16.0.6", {"center": v(13.41, -11.61) * mm, "radius": 0.5 * mm});
            skCircle(sketch, "E7.16.0.7", {"center": v(15.94, -11.61) * mm, "radius": 0.5 * mm});
            skCircle(sketch, "E7.16.0.8", {"center": v(-16.94, -11.61) * mm, "radius": 0.5 * mm});
            skCircle(sketch, "E7.16.0.9", {"center": v(-14.41, -11.61) * mm, "radius": 0.5 * mm});
            skCircle(sketch, "E7.16.0.10", {"center": v(-11.88, -11.61) * mm, "radius": 0.5 * mm});
            skCircle(sketch, "E7.16.0.11", {"center": v(-9.35, -11.61) * mm, "radius": 0.5 * mm});
            skCircle(sketch, "E7.16.0.12", {"center": v(-6.82, -11.61) * mm, "radius": 0.5 * mm});
            skCircle(sketch, "E7.16.0.13", {"center": v(-4.3, -11.61) * mm, "radius": 0.5 * mm});
            skCircle(sketch, "E7.16.0.14", {"center": v(-1.76, -11.61) * mm, "radius": 0.5 * mm});
            skLineSegment(sketch, "E7.16.0.15", {"start": v(-22, -11.61) * mm, "end": v(-19.47, -11.61) * mm, "construction": true});
            skCircle(sketch, "E7.16.0.16", {"center": v(21, -11.61) * mm, "radius": 0.5 * mm});
            skCircle(sketch, "E7.16.0.17", {"center": v(-22, -11.61) * mm, "radius": 0.5 * mm});
            skCircle(sketch, "E7.16.0.18", {"center": v(-19.47, -11.61) * mm, "radius": 0.5 * mm});
            skCircle(sketch, "E7.17.0.0", {"center": v(3.3, -14.14) * mm, "radius": 0.5 * mm});
            skCircle(sketch, "E7.17.0.1", {"center": v(5.82, -14.14) * mm, "radius": 0.5 * mm});
            skCircle(sketch, "E7.17.0.2", {"center": v(8.35, -14.14) * mm, "radius": 0.5 * mm});
            skCircle(sketch, "E7.17.0.3", {"center": v(18.47, -14.14) * mm, "radius": 0.5 * mm});
            skCircle(sketch, "E7.17.0.4", {"center": v(0.76, -14.14) * mm, "radius": 0.5 * mm});
            skCircle(sketch, "E7.17.0.5", {"center": v(10.88, -14.14) * mm, "radius": 0.5 * mm});
            skCircle(sketch, "E7.17.0.6", {"center": v(13.41, -14.14) * mm, "radius": 0.5 * mm});
            skCircle(sketch, "E7.17.0.7", {"center": v(15.94, -14.14) * mm, "radius": 0.5 * mm});
            skCircle(sketch, "E7.17.0.8", {"center": v(-16.94, -14.14) * mm, "radius": 0.5 * mm});
            skCircle(sketch, "E7.17.0.9", {"center": v(-14.41, -14.14) * mm, "radius": 0.5 * mm});
            skCircle(sketch, "E7.17.0.10", {"center": v(-11.88, -14.14) * mm, "radius": 0.5 * mm});
            skCircle(sketch, "E7.17.0.11", {"center": v(-9.35, -14.14) * mm, "radius": 0.5 * mm});
            skCircle(sketch, "E7.17.0.12", {"center": v(-6.82, -14.14) * mm, "radius": 0.5 * mm});
            skCircle(sketch, "E7.17.0.13", {"center": v(-4.3, -14.14) * mm, "radius": 0.5 * mm});
            skCircle(sketch, "E7.17.0.14", {"center": v(-1.76, -14.14) * mm, "radius": 0.5 * mm});
            skLineSegment(sketch, "E7.17.0.15", {"start": v(-22, -14.14) * mm, "end": v(-19.47, -14.14) * mm, "construction": true});
            skCircle(sketch, "E7.17.0.16", {"center": v(21, -14.14) * mm, "radius": 0.5 * mm});
            skCircle(sketch, "E7.17.0.17", {"center": v(-22, -14.14) * mm, "radius": 0.5 * mm});
            skCircle(sketch, "E7.17.0.18", {"center": v(-19.47, -14.14) * mm, "radius": 0.5 * mm});
            skCircle(sketch, "E7.18.0.0", {"center": v(3.3, -16.67) * mm, "radius": 0.5 * mm});
            skCircle(sketch, "E7.18.0.1", {"center": v(5.82, -16.67) * mm, "radius": 0.5 * mm});
            skCircle(sketch, "E7.18.0.2", {"center": v(8.35, -16.67) * mm, "radius": 0.5 * mm});
            skCircle(sketch, "E7.18.0.3", {"center": v(18.47, -16.67) * mm, "radius": 0.5 * mm});
            skCircle(sketch, "E7.18.0.4", {"center": v(0.76, -16.67) * mm, "radius": 0.5 * mm});
            skCircle(sketch, "E7.18.0.5", {"center": v(10.88, -16.67) * mm, "radius": 0.5 * mm});
            skCircle(sketch, "E7.18.0.6", {"center": v(13.41, -16.67) * mm, "radius": 0.5 * mm});
            skCircle(sketch, "E7.18.0.7", {"center": v(15.94, -16.67) * mm, "radius": 0.5 * mm});
            skCircle(sketch, "E7.18.0.8", {"center": v(-16.94, -16.67) * mm, "radius": 0.5 * mm});
            skCircle(sketch, "E7.18.0.9", {"center": v(-14.41, -16.67) * mm, "radius": 0.5 * mm});
            skCircle(sketch, "E7.18.0.10", {"center": v(-11.88, -16.67) * mm, "radius": 0.5 * mm});
            skCircle(sketch, "E7.18.0.11", {"center": v(-9.35, -16.67) * mm, "radius": 0.5 * mm});
            skCircle(sketch, "E7.18.0.12", {"center": v(-6.82, -16.67) * mm, "radius": 0.5 * mm});
            skCircle(sketch, "E7.18.0.13", {"center": v(-4.3, -16.67) * mm, "radius": 0.5 * mm});
            skCircle(sketch, "E7.18.0.14", {"center": v(-1.76, -16.67) * mm, "radius": 0.5 * mm});
            skLineSegment(sketch, "E7.18.0.15", {"start": v(-22, -16.67) * mm, "end": v(-19.47, -16.67) * mm, "construction": true});
            skCircle(sketch, "E7.18.0.16", {"center": v(21, -16.67) * mm, "radius": 0.5 * mm});
            skCircle(sketch, "E7.18.0.17", {"center": v(-22, -16.67) * mm, "radius": 0.5 * mm});
            skCircle(sketch, "E7.18.0.18", {"center": v(-19.47, -16.67) * mm, "radius": 0.5 * mm});
            skCircle(sketch, "E7.19.0.0", {"center": v(3.3, -19.2) * mm, "radius": 0.5 * mm});
            skCircle(sketch, "E7.19.0.1", {"center": v(5.82, -19.2) * mm, "radius": 0.5 * mm});
            skCircle(sketch, "E7.19.0.2", {"center": v(8.35, -19.2) * mm, "radius": 0.5 * mm});
            skCircle(sketch, "E7.19.0.3", {"center": v(18.47, -19.2) * mm, "radius": 0.5 * mm});
            skCircle(sketch, "E7.19.0.4", {"center": v(0.76, -19.2) * mm, "radius": 0.5 * mm});
            skCircle(sketch, "E7.19.0.5", {"center": v(10.88, -19.2) * mm, "radius": 0.5 * mm});
            skCircle(sketch, "E7.19.0.6", {"center": v(13.41, -19.2) * mm, "radius": 0.5 * mm});
            skCircle(sketch, "E7.19.0.7", {"center": v(15.94, -19.2) * mm, "radius": 0.5 * mm});
            skCircle(sketch, "E7.19.0.8", {"center": v(-16.94, -19.2) * mm, "radius": 0.5 * mm});
            skCircle(sketch, "E7.19.0.9", {"center": v(-14.41, -19.2) * mm, "radius": 0.5 * mm});
            skCircle(sketch, "E7.19.0.10", {"center": v(-11.88, -19.2) * mm, "radius": 0.5 * mm});
            skCircle(sketch, "E7.19.0.11", {"center": v(-9.35, -19.2) * mm, "radius": 0.5 * mm});
            skCircle(sketch, "E7.19.0.12", {"center": v(-6.82, -19.2) * mm, "radius": 0.5 * mm});
            skCircle(sketch, "E7.19.0.13", {"center": v(-4.3, -19.2) * mm, "radius": 0.5 * mm});
            skCircle(sketch, "E7.19.0.14", {"center": v(-1.76, -19.2) * mm, "radius": 0.5 * mm});
            skLineSegment(sketch, "E7.19.0.15", {"start": v(-22, -19.2) * mm, "end": v(-19.47, -19.2) * mm, "construction": true});
            skCircle(sketch, "E7.19.0.16", {"center": v(21, -19.2) * mm, "radius": 0.5 * mm});
            skCircle(sketch, "E7.19.0.17", {"center": v(-22, -19.2) * mm, "radius": 0.5 * mm});
            skCircle(sketch, "E7.19.0.18", {"center": v(-19.47, -19.2) * mm, "radius": 0.5 * mm});
            skCircle(sketch, "E7.20.0.0", {"center": v(3.3, -21.73) * mm, "radius": 0.5 * mm});
            skCircle(sketch, "E7.20.0.1", {"center": v(5.82, -21.73) * mm, "radius": 0.5 * mm});
            skCircle(sketch, "E7.20.0.2", {"center": v(8.35, -21.73) * mm, "radius": 0.5 * mm});
            skCircle(sketch, "E7.20.0.3", {"center": v(18.47, -21.73) * mm, "radius": 0.5 * mm});
            skCircle(sketch, "E7.20.0.4", {"center": v(0.76, -21.73) * mm, "radius": 0.5 * mm});
            skCircle(sketch, "E7.20.0.5", {"center": v(10.88, -21.73) * mm, "radius": 0.5 * mm});
            skCircle(sketch, "E7.20.0.6", {"center": v(13.41, -21.73) * mm, "radius": 0.5 * mm});
            skCircle(sketch, "E7.20.0.7", {"center": v(15.94, -21.73) * mm, "radius": 0.5 * mm});
            skCircle(sketch, "E7.20.0.8", {"center": v(-16.94, -21.73) * mm, "radius": 0.5 * mm});
            skCircle(sketch, "E7.20.0.9", {"center": v(-14.41, -21.73) * mm, "radius": 0.5 * mm});
            skCircle(sketch, "E7.20.0.10", {"center": v(-11.88, -21.73) * mm, "radius": 0.5 * mm});
            skCircle(sketch, "E7.20.0.11", {"center": v(-9.35, -21.73) * mm, "radius": 0.5 * mm});
            skCircle(sketch, "E7.20.0.12", {"center": v(-6.82, -21.73) * mm, "radius": 0.5 * mm});
            skCircle(sketch, "E7.20.0.13", {"center": v(-4.3, -21.73) * mm, "radius": 0.5 * mm});
            skCircle(sketch, "E7.20.0.14", {"center": v(-1.76, -21.73) * mm, "radius": 0.5 * mm});
            skLineSegment(sketch, "E7.20.0.15", {"start": v(-22, -21.73) * mm, "end": v(-19.47, -21.73) * mm, "construction": true});
            skCircle(sketch, "E7.20.0.16", {"center": v(21, -21.73) * mm, "radius": 0.5 * mm});
            skCircle(sketch, "E7.20.0.17", {"center": v(-22, -21.73) * mm, "radius": 0.5 * mm});
            skCircle(sketch, "E7.20.0.18", {"center": v(-19.47, -21.73) * mm, "radius": 0.5 * mm});
            skCircle(sketch, "E7.21.0.0", {"center": v(3.3, -24.26) * mm, "radius": 0.5 * mm});
            skCircle(sketch, "E7.21.0.1", {"center": v(5.82, -24.26) * mm, "radius": 0.5 * mm});
            skCircle(sketch, "E7.21.0.2", {"center": v(8.35, -24.26) * mm, "radius": 0.5 * mm});
            skCircle(sketch, "E7.21.0.3", {"center": v(18.47, -24.26) * mm, "radius": 0.5 * mm});
            skCircle(sketch, "E7.21.0.4", {"center": v(0.76, -24.26) * mm, "radius": 0.5 * mm});
            skCircle(sketch, "E7.21.0.5", {"center": v(10.88, -24.26) * mm, "radius": 0.5 * mm});
            skCircle(sketch, "E7.21.0.6", {"center": v(13.41, -24.26) * mm, "radius": 0.5 * mm});
            skCircle(sketch, "E7.21.0.7", {"center": v(15.94, -24.26) * mm, "radius": 0.5 * mm});
            skCircle(sketch, "E7.21.0.8", {"center": v(-16.94, -24.26) * mm, "radius": 0.5 * mm});
            skCircle(sketch, "E7.21.0.9", {"center": v(-14.41, -24.26) * mm, "radius": 0.5 * mm});
            skCircle(sketch, "E7.21.0.10", {"center": v(-11.88, -24.26) * mm, "radius": 0.5 * mm});
            skCircle(sketch, "E7.21.0.11", {"center": v(-9.35, -24.26) * mm, "radius": 0.5 * mm});
            skCircle(sketch, "E7.21.0.12", {"center": v(-6.82, -24.26) * mm, "radius": 0.5 * mm});
            skCircle(sketch, "E7.21.0.13", {"center": v(-4.3, -24.26) * mm, "radius": 0.5 * mm});
            skCircle(sketch, "E7.21.0.14", {"center": v(-1.76, -24.26) * mm, "radius": 0.5 * mm});
            skLineSegment(sketch, "E7.21.0.15", {"start": v(-22, -24.26) * mm, "end": v(-19.47, -24.26) * mm, "construction": true});
            skCircle(sketch, "E7.21.0.16", {"center": v(21, -24.26) * mm, "radius": 0.5 * mm});
            skCircle(sketch, "E7.21.0.17", {"center": v(-22, -24.26) * mm, "radius": 0.5 * mm});
            skCircle(sketch, "E7.21.0.18", {"center": v(-19.47, -24.26) * mm, "radius": 0.5 * mm});
            skCircle(sketch, "E7.22.0.0", {"center": v(3.3, -26.79) * mm, "radius": 0.5 * mm});
            skCircle(sketch, "E7.22.0.1", {"center": v(5.82, -26.79) * mm, "radius": 0.5 * mm});
            skCircle(sketch, "E7.22.0.2", {"center": v(8.35, -26.79) * mm, "radius": 0.5 * mm});
            skCircle(sketch, "E7.22.0.3", {"center": v(18.47, -26.79) * mm, "radius": 0.5 * mm});
            skCircle(sketch, "E7.22.0.4", {"center": v(0.76, -26.79) * mm, "radius": 0.5 * mm});
            skCircle(sketch, "E7.22.0.5", {"center": v(10.88, -26.79) * mm, "radius": 0.5 * mm});
            skCircle(sketch, "E7.22.0.6", {"center": v(13.41, -26.79) * mm, "radius": 0.5 * mm});
            skCircle(sketch, "E7.22.0.7", {"center": v(15.94, -26.79) * mm, "radius": 0.5 * mm});
            skCircle(sketch, "E7.22.0.8", {"center": v(-16.94, -26.79) * mm, "radius": 0.5 * mm});
            skCircle(sketch, "E7.22.0.9", {"center": v(-14.41, -26.79) * mm, "radius": 0.5 * mm});
            skCircle(sketch, "E7.22.0.10", {"center": v(-11.88, -26.79) * mm, "radius": 0.5 * mm});
            skCircle(sketch, "E7.22.0.11", {"center": v(-9.35, -26.79) * mm, "radius": 0.5 * mm});
            skCircle(sketch, "E7.22.0.12", {"center": v(-6.82, -26.79) * mm, "radius": 0.5 * mm});
            skCircle(sketch, "E7.22.0.13", {"center": v(-4.3, -26.79) * mm, "radius": 0.5 * mm});
            skCircle(sketch, "E7.22.0.14", {"center": v(-1.76, -26.79) * mm, "radius": 0.5 * mm});
            skLineSegment(sketch, "E7.22.0.15", {"start": v(-22, -26.79) * mm, "end": v(-19.47, -26.79) * mm, "construction": true});
            skCircle(sketch, "E7.22.0.16", {"center": v(21, -26.79) * mm, "radius": 0.5 * mm});
            skCircle(sketch, "E7.22.0.17", {"center": v(-22, -26.79) * mm, "radius": 0.5 * mm});
            skCircle(sketch, "E7.22.0.18", {"center": v(-19.47, -26.79) * mm, "radius": 0.5 * mm});
            skCircle(sketch, "E7.23.0.0", {"center": v(3.3, -29.32) * mm, "radius": 0.5 * mm});
            skCircle(sketch, "E7.23.0.1", {"center": v(5.82, -29.32) * mm, "radius": 0.5 * mm});
            skCircle(sketch, "E7.23.0.2", {"center": v(8.35, -29.32) * mm, "radius": 0.5 * mm});
            skCircle(sketch, "E7.23.0.3", {"center": v(18.47, -29.32) * mm, "radius": 0.5 * mm});
            skCircle(sketch, "E7.23.0.4", {"center": v(0.76, -29.32) * mm, "radius": 0.5 * mm});
            skCircle(sketch, "E7.23.0.5", {"center": v(10.88, -29.32) * mm, "radius": 0.5 * mm});
            skCircle(sketch, "E7.23.0.6", {"center": v(13.41, -29.32) * mm, "radius": 0.5 * mm});
            skCircle(sketch, "E7.23.0.7", {"center": v(15.94, -29.32) * mm, "radius": 0.5 * mm});
            skCircle(sketch, "E7.23.0.8", {"center": v(-16.94, -29.32) * mm, "radius": 0.5 * mm});
            skCircle(sketch, "E7.23.0.9", {"center": v(-14.41, -29.32) * mm, "radius": 0.5 * mm});
            skCircle(sketch, "E7.23.0.10", {"center": v(-11.88, -29.32) * mm, "radius": 0.5 * mm});
            skCircle(sketch, "E7.23.0.11", {"center": v(-9.35, -29.32) * mm, "radius": 0.5 * mm});
            skCircle(sketch, "E7.23.0.12", {"center": v(-6.82, -29.32) * mm, "radius": 0.5 * mm});
            skCircle(sketch, "E7.23.0.13", {"center": v(-4.3, -29.32) * mm, "radius": 0.5 * mm});
            skCircle(sketch, "E7.23.0.14", {"center": v(-1.76, -29.32) * mm, "radius": 0.5 * mm});
            skLineSegment(sketch, "E7.23.0.15", {"start": v(-22, -29.32) * mm, "end": v(-19.47, -29.32) * mm, "construction": true});
            skCircle(sketch, "E7.23.0.16", {"center": v(21, -29.32) * mm, "radius": 0.5 * mm});
            skCircle(sketch, "E7.23.0.17", {"center": v(-22, -29.32) * mm, "radius": 0.5 * mm});
            skCircle(sketch, "E7.23.0.18", {"center": v(-19.47, -29.32) * mm, "radius": 0.5 * mm});
            skLineSegment(sketch, "E7.direction1", {"start": v(21, 28.85) * mm, "end": v(21, 26.32) * mm, "construction": true});
            skSolve(sketch);
        }
        {
            var Q0;
            Q0 = qSketchRegion(id + "F2", true);
            extrude(context, id + "F3", {"entities" : qUnion([Q0]), "operationType" : NewBodyOperationType.REMOVE, "depth" : 25 * mm});
        }
        {
            var Q0;
            Q0=makeQuery(id+"F1.opExtrude","CAP_FACE",FACE,{"disambiguationData":[OSD([sQuery(id+"F0.wireOp",EDGE,"E0.bottom"),sQuery(id+"F0.wireOp",EDGE,"E0.top"),sQuery(id+"F0.wireOp",EDGE,"E0.left"),sQuery(id+"F0.wireOp",EDGE,"E0.right"),sQuery(id+"F0.wireOp",EDGE,"E1"),sQuery(id+"F0.wireOp",EDGE,"E2"),sQuery(id+"F0.wireOp",EDGE,"E3"),sQuery(id+"F0.wireOp",EDGE,"E4")])],"isStart":false});
            var sketch = newSketch(context, id + "F4", { "sketchPlane" : qUnion([Q0])});
            skLineSegment(sketch, "E8.bottom", {"start": v(38.7, 46.3) * mm, "end": v(40.45, 46.3) * mm});
            skLineSegment(sketch, "E8.top", {"start": v(38.7, 45.3) * mm, "end": v(40.45, 45.3) * mm});
            skLineSegment(sketch, "E8.left", {"start": v(38.7, 46.3) * mm, "end": v(38.7, 45.3) * mm});
            skLineSegment(sketch, "E8.right", {"start": v(40.45, 46.3) * mm, "end": v(40.45, 45.3) * mm});
            skLineSegment(sketch, "E9.bottom", {"start": v(-25.5, 35.25) * mm, "end": v(4.5, 35.25) * mm});
            skLineSegment(sketch, "E9.top", {"start": v(-25.5, 5.25) * mm, "end": v(4.5, 5.25) * mm});
            skLineSegment(sketch, "E9.left", {"start": v(-25.5, 35.25) * mm, "end": v(-25.5, 5.25) * mm});
            skLineSegment(sketch, "E9.right", {"start": v(4.5, 35.25) * mm, "end": v(4.5, 5.25) * mm});
            skSolve(sketch);
        }
        {
            var Q0;
            Q0 = qSketchRegion(id + "F4", true);
            extrude(context, id + "F5", {"entities" : qUnion([Q0]), "operationType" : NewBodyOperationType.REMOVE, "oppositeDirection" : true, "depth" : 5 * mm});
        }
    });
